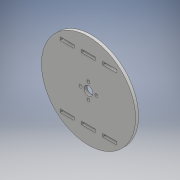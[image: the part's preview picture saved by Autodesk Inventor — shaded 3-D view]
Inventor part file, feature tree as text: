
AUTODESK INVENTOR PART (.ipt)
format: ipt  version: 2018 (Build 220112000, 112)  size: 142,848 bytes
history: native  units: mm
features: extrude x3, sketch x3, other x1
ambient origin geometry x8: Origin, YZ Plane, XZ Plane, XY Plane, X Axis, Y Axis, Z Axis, Center Point
bodies: Body1 (feature_tree)
feature tree (7):
  other  "Sólido1"
  extrude  "Extrusión1"  Depth=3.0mm
  extrude  "Extrusión2"  Depth=10.0mm
  extrude  "Extrusión3"  [1 undecoded]
  sketch  "Boceto1"  dims[d19=3.0mm d20=0.0mm d23=7.0mm]
  sketch  "Boceto2"  dims[d24=10.0mm d25=0.0mm d26=9.0mm]
  sketch  "Boceto3"  dims[d27=10.0mm d28=0.0mm]
note: 1 required parameter value undecoded (feature->parameter linkage not recoverable at this tier; creation-order binding heuristic only, values carry confidence <= 0.55)
